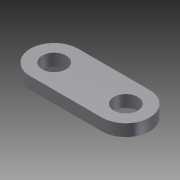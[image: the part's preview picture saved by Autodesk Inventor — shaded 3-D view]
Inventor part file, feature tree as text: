
AUTODESK INVENTOR PART (.ipt)
format: ipt  version: 2011 SP1 (Build 150282100, 282)  size: 81,408 bytes
history: native  units: mm
features: extrude x1, sketch x1
ambient origin geometry x8: Origin, YZ Plane, XZ Plane, XY Plane, X Axis, Y Axis, Z Axis, Center Point
bodies: Solid1 (feature_tree)
feature tree (2):
  extrude  "Extrusion1"  Depth=20.0mm
  sketch  "Sketch1"  dims[d0=20.0mm d1=20.0mm d2=30.0mm d3=10.0mm d4=10.0mm d5=5.0mm d6=0.0mm]
